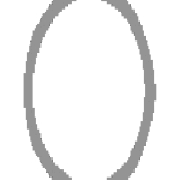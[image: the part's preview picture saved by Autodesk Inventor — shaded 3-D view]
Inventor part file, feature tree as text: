
AUTODESK INVENTOR PART (.ipt)
format: ipt  version: 2021 (Build 250183000, 183)  size: 112,640 bytes
history: native  units: in
note: dims shown in document units (in); Inventor stores cm internally (conversion verified against a paired STEP export)
features: other x4, sketch x3, plane x1
ambient origin geometry x8: Origin, YZ Plane, XZ Plane, XY Plane, X Axis, Y Axis, Z Axis, Center Point
bodies: Solid1 (feature_tree), Body (feature_tree)
feature tree (8):
  other  "Driven Length"
  other  "Frame Generator"
  other  "Start Plane"
  other  "End Plane"
  sketch  "Sketch"  dims[d2=3.5in d4=-0.0in d5=3.5in d6=0.12in d7=0.0in d8=90.0deg d9=3.5in]
  sketch  "Sketch2"  dims[d0=1.0in]
  plane  "Work Plane3"
  sketch  "Sketch3"  dims[d1=0.065in]
